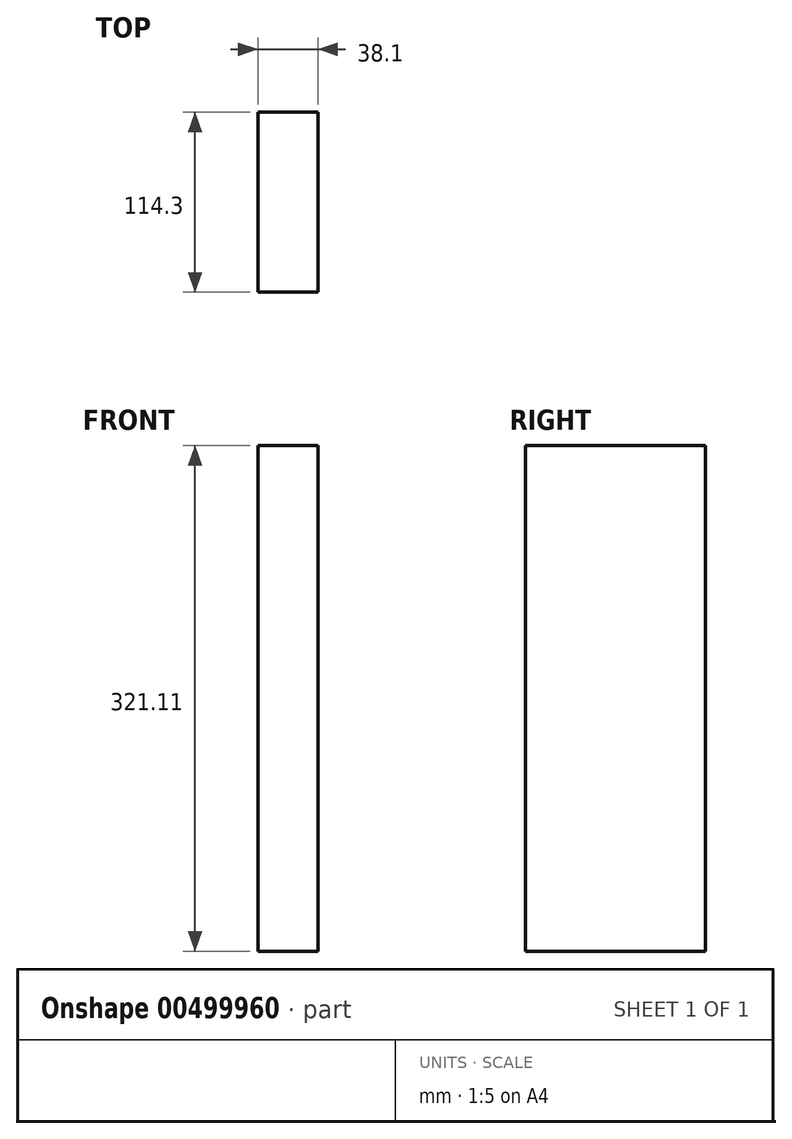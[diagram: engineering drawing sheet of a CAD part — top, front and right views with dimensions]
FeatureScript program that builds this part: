
annotation { "Feature Type Name" : "Feature", "Feature Type Description" : "" }
export const myFeature = defineFeature(function(context is Context, id is Id, definition is map)
    precondition{}
    {
        {
            var Q0;
            Q0=qCreatedBy(makeId("Front.planeOp"),FACE);
            var sketch = newSketch(context, id + "F0", { "sketchPlane" : qUnion([Q0])});
            skLineSegment(sketch, "E0.bottom", {"start": v(-101.6, 1154) * mm, "end": v(101.6, 1154) * mm});
            skLineSegment(sketch, "E0.top", {"start": v(-101.6, -1154) * mm, "end": v(101.6, -1154) * mm});
            skLineSegment(sketch, "E0.left", {"start": v(-101.6, 1154) * mm, "end": v(-101.6, -1154) * mm});
            skLineSegment(sketch, "E0.right", {"start": v(101.6, 1154) * mm, "end": v(101.6, -1154) * mm});
            skPoint(sketch, "E0.middle", {"position": v(0, 0) * mm});
            skLineSegment(sketch, "E1", {"start": v(-101.6, -912.7) * mm, "end": v(101.6, -912.7) * mm});
            skLineSegment(sketch, "E2.bottom", {"start": v(-63.5, -1154) * mm, "end": v(-25.4, -1154) * mm});
            skLineSegment(sketch, "E2.top", {"start": v(-63.5, -912.7) * mm, "end": v(-25.4, -912.7) * mm});
            skLineSegment(sketch, "E2.left", {"start": v(-63.5, -1154) * mm, "end": v(-63.5, -912.7) * mm});
            skLineSegment(sketch, "E2.right", {"start": v(-25.4, -1154) * mm, "end": v(-25.4, -912.7) * mm});
            skLineSegment(sketch, "E3", {"start": v(-101.6, 1039.7) * mm, "end": v(101.6, 1039.7) * mm});
            skLineSegment(sketch, "E4.bottom", {"start": v(-25.4, 1039.7) * mm, "end": v(25.4, 1039.7) * mm});
            skLineSegment(sketch, "E4.top", {"start": v(-25.4, 1154) * mm, "end": v(25.4, 1154) * mm});
            skLineSegment(sketch, "E4.left", {"start": v(-25.4, 1039.7) * mm, "end": v(-25.4, 1154) * mm});
            skLineSegment(sketch, "E4.right", {"start": v(25.4, 1039.7) * mm, "end": v(25.4, 1154) * mm});
            skLineSegment(sketch, "E5.bottom", {"start": v(-50.8, 430.1) * mm, "end": v(-12.7, 430.1) * mm});
            skLineSegment(sketch, "E5.top", {"start": v(-50.8, 751.2) * mm, "end": v(-12.7, 751.2) * mm});
            skLineSegment(sketch, "E5.left", {"start": v(-50.8, 430.1) * mm, "end": v(-50.8, 751.2) * mm});
            skLineSegment(sketch, "E5.right", {"start": v(-12.7, 430.1) * mm, "end": v(-12.7, 751.2) * mm});
            skSolve(sketch);
        }
        {
            var Q0;
            {var subQ3=sQuery(id+"F0.wireOp",EDGE,"E2.top");Q0=makeQuery(id+"F0.imprint","IMPRINT",FACE,{"disambiguationData":[TD([[makeQuery(id+"F0.imprint","IMPRINT",EDGE,{"derivedFrom":subQ3}),1.0]])]});}
            var Q1;
            Q1=makeQuery(id+"F0.imprint","IMPRINT",FACE,{"disambiguationData":[TD([[makeQuery(id+"F0.imprint","IMPRINT",EDGE,{"derivedFrom":sQuery(id+"F0.wireOp",EDGE,"E4.bottom")}),1.0]])]});
            var Q2;
            Q2=makeQuery(id+"F0.imprint","IMPRINT",FACE,{"disambiguationData":[TD([[makeQuery(id+"F0.imprint","IMPRINT",EDGE,{"derivedFrom":sQuery(id+"F0.wireOp",EDGE,"E2.bottom")}),1.0]])]});
            var Q3;
            Q3=makeQuery(id+"F0.imprint","IMPRINT",FACE,{"disambiguationData":[TD([[makeQuery(id+"F0.imprint","IMPRINT",EDGE,{"derivedFrom":sQuery(id+"F0.wireOp",EDGE,"E5.bottom")}),1.0]])]});
            var Q4;
            {var subQ2=sQuery(id+"F0.wireOp",EDGE,"fFLy5hLs-ibyj-m66z-IQ5R-tNvOscupj2RI");Q4=makeQuery(id+"F0.imprint","IMPRINT",FACE,{"disambiguationData":[TD([[makeQuery(id+"F0.imprint","IMPRINT",EDGE,{"derivedFrom":subQ2}),-1.0]])]});}
            extrude(context, id + "F1", {"entities" : qUnion([Q0, Q1, Q2, Q3, Q4]), "oppositeDirection" : true, "depth" : 203.2 * mm, "offsetDistance" : 25.4 * mm});
        }
        {
            var Q0;
            Q0=makeQuery(id+"F0.imprint","IMPRINT",FACE,{"disambiguationData":[TD([[makeQuery(id+"F0.imprint","IMPRINT",EDGE,{"derivedFrom":sQuery(id+"F0.wireOp",EDGE,"E5.bottom")}),1.0]])]});
            extrude(context, id + "F2", {"entities" : qUnion([Q0]), "operationType" : NewBodyOperationType.REMOVE, "oppositeDirection" : true, "depth" : 88.9 * mm});
        }
    });
